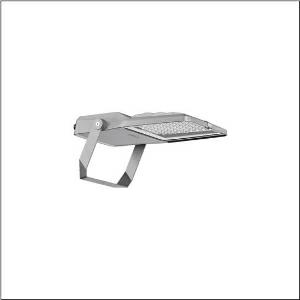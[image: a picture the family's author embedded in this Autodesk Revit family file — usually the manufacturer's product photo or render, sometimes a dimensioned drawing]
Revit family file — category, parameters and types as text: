
# Revit family: floodlight_fl_21_iq_mini___pl33t_5xa7772d5f1a_ae39
name_source: partatom
category: Lighting Fixtures
units: mm (PartAtom-declared; Revit-internal decimal feet)

## family parameters
Cut with Voids When Loaded = No
Host = Face
Light Source = No
Part Type = Normal
Room Calculation Point = No
Round Connector Dimension = Use Diameter
Shared = No

## types (1)
- --- (1 x LED, 16450 lm, 143 W, 4000K)
    Apparent Load = 143 VA
    CIE Flux Codes = 26 75 99 100 100
    Color Rendering = 80
    Color Temperature = 4000K
    Default Elevation = 1800 mm
    Description = Floodlight FL 21 iQ mini, floodlight, primary light control with lens, of PMMA, primary optical cover: protective disc, of toughened safety glass, transparent, light distribution: PL33T, light emission: direct distribution, installation type: surface-mounted, LED, High Power LED, rated luminous flux: 16.450lm, luminous efficacy: 115lm/W, light colour: 840, colour temperature: 4000K, control gear: iQ Street-Remote/DALI, control: Street-Remote, Auto-Match, Temp-Guard, Night-Set, Smart-Wire, Desk-Remote (wireless, voltage-free reading and setting of iQ features in the workshop via application-optimized NFC function/RFID function), optimised constant luminous flux control (CLO 2.0), with terminal, 6-pole, mains connection: 220..240V, AC, 50/60Hz, start of lifetime: 143W, end of service life: 152W, reduction: 61W, luminaire housing, of diecast aluminium, powder-coated, Siteco® metallic grey (DB 702S), corrosivity category C5 mid according to DIN EN ISO 12944, suitable for swimming pools, chlorine-resistant, sealing non-destructively replaceable, mounting bracket, of steel, galvanised, powder-coated, Siteco® metallic grey (DB 702S), protection rating (complete): IP66, insulation class (complete): insulation class II (safety insulation), certification: CE, ENEC, VDE, protection symbol: D, impact resistance: IK08, permissible operating ambient temperature: -40..+40°C, permissible operating ambient temperature for outdoor applications: -40..+50°C, standard: DIN EN 12944, LABS conformity tested according to VDMA 24364:2018-05, packaging unit: 1 piece

Light Distribution: PL33T
    Height = 70 mm
    Lamp = 1 x LED
    Lamp Light Flux = 16450 lm
    Lamp Power = 143 W
    Lamp count = 1
    Length = 485 mm
    Luminous efficacy = 115 lm/W
    Manufacturer = Siteco
    ModVariant = No
    Model = 5XA7772D5F1A
    Number of Poles = 1
    OnlyDefault = Yes
    Power Factor = 1
    Product Name = Floodlight FL 21 iQ mini | PL33T
    Product group = floodlight | pylon annexe
    ProductGroupID = 6201
    Protection Class = Protection class II
    Protection Degree = IP 66
    RLX_Detail_Level = 1
    RLX_Emergency_Light_Flux = 0 lm
    RLX_Emergency_Type = 0
    RLX_Emergency_Type_DB = No
    RlxData = <blob elided: 96433 chars, md5=a312c352>
    Socket = socket
    Standby Power = 0 W
    System Light Flux = 16450 lm
    System Power = 143 W
    Type Comments = factory setting: luminous flux: 100 % | dim-lin: 254 | 730 mA
    Type Image = l_1006845.jpg
    URL = http://relux.com
    VarID = @adj_170183
    Voltage = 0 V
    Weight = 0.00 kg
    Width = 337 mm

## geometry (parser evidence)
native form markers: Blend x4, Sweep x12
no freeform markers — native parametric forms only
